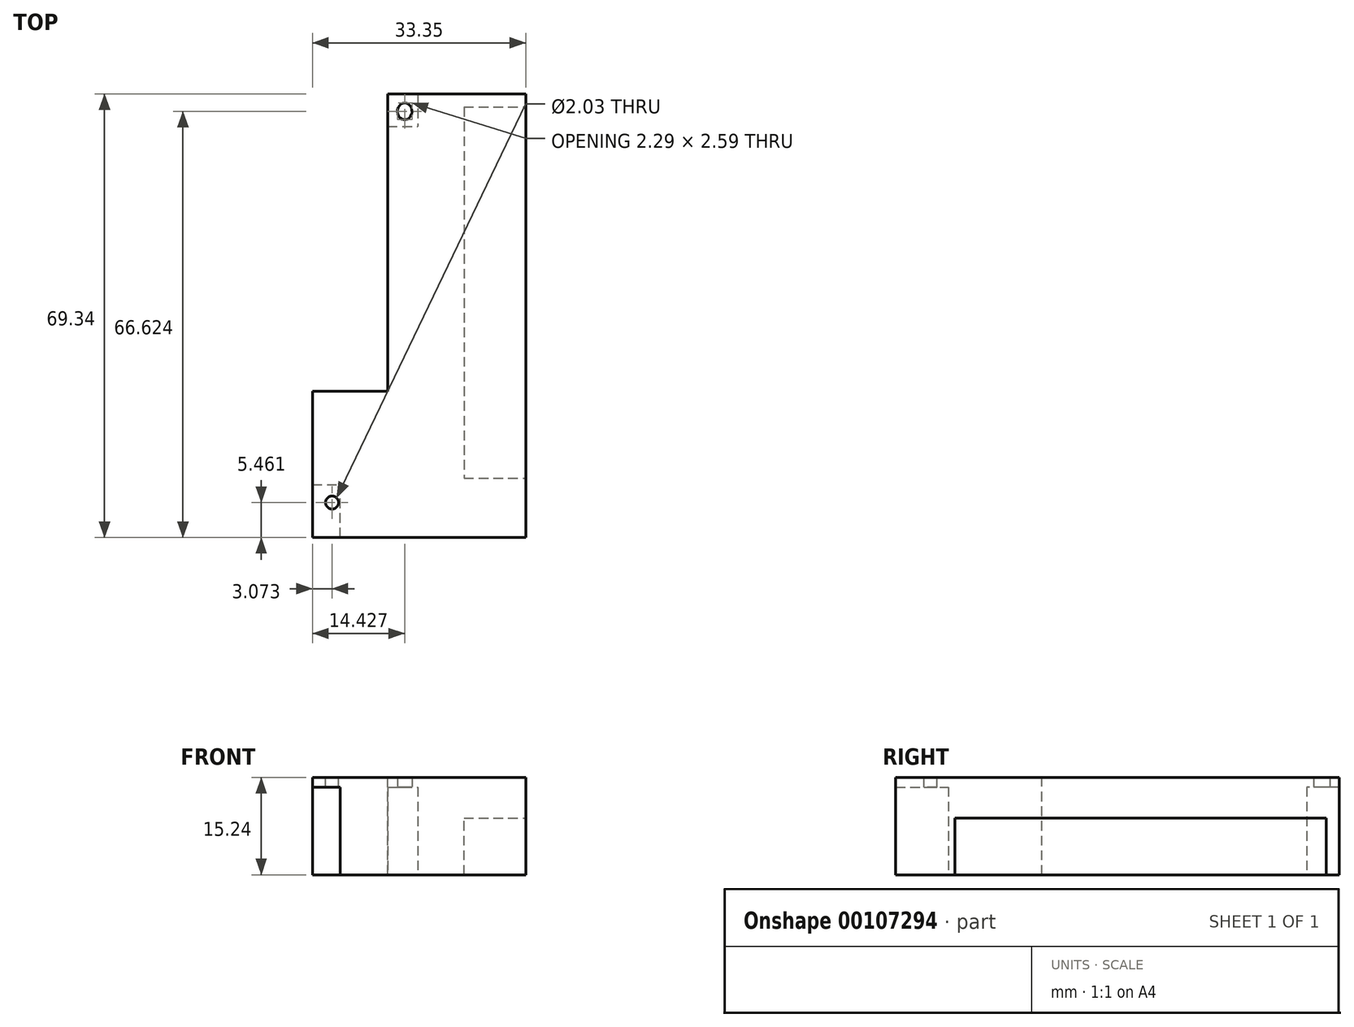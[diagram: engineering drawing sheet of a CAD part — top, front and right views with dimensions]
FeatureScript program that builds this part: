
annotation { "Feature Type Name" : "Feature", "Feature Type Description" : "" }
export const myFeature = defineFeature(function(context is Context, id is Id, definition is map)
    precondition{}
    {
        {
            var Q0;
            Q0=qCreatedBy(makeId("Top.planeOp"),FACE);
            var sketch = newSketch(context, id + "F0", { "sketchPlane" : qUnion([Q0])});
            skLineSegment(sketch, "E0.bottom", {"start": v(-21.6, 69.34) * mm, "end": v(0, 69.34) * mm});
            skLineSegment(sketch, "E0.top", {"start": v(-21.6, 0) * mm, "end": v(0, 0) * mm});
            skLineSegment(sketch, "E0.left", {"start": v(-21.6, 69.34) * mm, "end": v(-21.6, 22.86) * mm});
            skLineSegment(sketch, "E0.right", {"start": v(0, 69.34) * mm, "end": v(0, 0) * mm});
            skLineSegment(sketch, "E1.bottom", {"start": v(-21.6, 0) * mm, "end": v(-33.35, 0) * mm});
            skLineSegment(sketch, "E1.top", {"start": v(-21.6, 22.86) * mm, "end": v(-33.35, 22.86) * mm});
            skLineSegment(sketch, "E1.right", {"start": v(-33.35, 0) * mm, "end": v(-33.35, 22.86) * mm});
            skCircle(sketch, "E2", {"center": v(-30.28, 5.46) * mm, "radius": 1.02 * mm});
            skLineSegment(sketch, "E3", {"start": v(-33.35, 9.14) * mm, "end": v(0, 9.14) * mm});
            skEllipse(sketch, "E4", {"center": v(-18.92, 66.62) * mm, "majorRadius": 1.3 * mm, "minorRadius": 1.14 * mm, "majorAxis": v(0, 1)});
            skSolve(sketch);
        }
        {
            var Q0;
            {var subQ2=sQuery(id+"F0.wireOp",EDGE,"E0.bottom");Q0=makeQuery(id+"F0.imprint","IMPRINT",FACE,{"disambiguationData":[TD([[makeQuery(id+"F0.imprint","IMPRINT",EDGE,{"derivedFrom":subQ2}),-1.0]])]});}
            var Q1;
            {var subQ4=sQuery(id+"F0.wireOp",EDGE,"E0.top");Q1=makeQuery(id+"F0.imprint","IMPRINT",FACE,{"disambiguationData":[TD([[makeQuery(id+"F0.imprint","IMPRINT",EDGE,{"derivedFrom":subQ4}),1.0]])]});}
            extrude(context, id + "F1", {"entities" : qUnion([Q0, Q1]), "oppositeDirection" : true, "depth" : 15.24 * mm});
        }
        {
            var Q0;
            Q0=makeQuery(id+"F1.opExtrude","CAP_FACE",FACE,{"disambiguationData":[OSD([sQuery(id+"F0.wireOp",EDGE,"E0.bottom"),sQuery(id+"F0.wireOp",EDGE,"E0.top"),sQuery(id+"F0.wireOp",EDGE,"E0.left"),sQuery(id+"F0.wireOp",EDGE,"E0.right"),sQuery(id+"F0.wireOp",EDGE,"E1.bottom"),sQuery(id+"F0.wireOp",EDGE,"E1.top"),sQuery(id+"F0.wireOp",EDGE,"E1.right"),sQuery(id+"F0.wireOp",EDGE,"E2"),sQuery(id+"F0.wireOp",EDGE,"E4")])],"isStart":false});
            var sketch = newSketch(context, id + "F2", { "sketchPlane" : qUnion([Q0])});
            skLineSegment(sketch, "E5.bottom", {"start": v(-33.35, 0) * mm, "end": v(-29.03, 0) * mm});
            skLineSegment(sketch, "E5.top", {"start": v(-33.35, -8.26) * mm, "end": v(-29.03, -8.26) * mm});
            skLineSegment(sketch, "E5.left", {"start": v(-33.35, 0) * mm, "end": v(-33.35, -8.26) * mm});
            skLineSegment(sketch, "E5.right", {"start": v(-29.03, 0) * mm, "end": v(-29.03, -8.26) * mm});
            skSolve(sketch);
        }
        {
            var Q0;
            Q0=makeQuery(id+"F2.imprint","IMPRINT",FACE,{"disambiguationData":[TD([[makeQuery(id+"F2.imprint","IMPRINT",EDGE,{"derivedFrom":sQuery(id+"F2.wireOp",EDGE,"E5.bottom")}),1.0]])]});
            extrude(context, id + "F3", {"entities" : qUnion([Q0]), "operationType" : NewBodyOperationType.REMOVE, "oppositeDirection" : true, "depth" : 13.72 * mm});
        }
        {
            var Q0;
            Q0=makeQuery(id+"F1.opExtrude","CAP_FACE",FACE,{"disambiguationData":[OSD([sQuery(id+"F0.wireOp",EDGE,"E0.bottom"),sQuery(id+"F0.wireOp",EDGE,"E0.top"),sQuery(id+"F0.wireOp",EDGE,"E0.left"),sQuery(id+"F0.wireOp",EDGE,"E0.right"),sQuery(id+"F0.wireOp",EDGE,"E1.bottom"),sQuery(id+"F0.wireOp",EDGE,"E1.top"),sQuery(id+"F0.wireOp",EDGE,"E1.right"),sQuery(id+"F0.wireOp",EDGE,"E2"),sQuery(id+"F0.wireOp",EDGE,"E4")])],"isStart":false});
            var sketch = newSketch(context, id + "F4", { "sketchPlane" : qUnion([Q0])});
            skLineSegment(sketch, "E6.bottom", {"start": v(-21.6, -69.34) * mm, "end": v(-16.9, -69.34) * mm});
            skLineSegment(sketch, "E6.top", {"start": v(-21.6, -64.26) * mm, "end": v(-16.9, -64.26) * mm});
            skLineSegment(sketch, "E6.left", {"start": v(-21.6, -69.34) * mm, "end": v(-21.6, -64.26) * mm});
            skLineSegment(sketch, "E6.right", {"start": v(-16.9, -69.34) * mm, "end": v(-16.9, -64.26) * mm});
            skSolve(sketch);
        }
        {
            var Q0;
            Q0=qSketchRegion(id+"F4",true);
            extrude(context, id + "F5", {"entities" : qUnion([Q0]), "operationType" : NewBodyOperationType.REMOVE, "oppositeDirection" : true, "depth" : 13.72 * mm});
        }
        {
            var Q0;
            Q0=makeQuery(id+"F1.opExtrude","SWEPT_FACE",FACE,{"disambiguationData":[OSD([sQuery(id+"F0.wireOp",EDGE,"E0.right")])]});
            var sketch = newSketch(context, id + "F6", { "sketchPlane" : qUnion([Q0])});
            skLineSegment(sketch, "E7.bottom", {"start": v(9.27, -15.24) * mm, "end": v(67.3, -15.24) * mm});
            skLineSegment(sketch, "E7.top", {"start": v(9.27, -6.35) * mm, "end": v(67.3, -6.35) * mm});
            skLineSegment(sketch, "E7.left", {"start": v(9.27, -15.24) * mm, "end": v(9.27, -6.35) * mm});
            skLineSegment(sketch, "E7.right", {"start": v(67.3, -15.24) * mm, "end": v(67.3, -6.35) * mm});
            skSolve(sketch);
        }
        {
            var Q0;
            Q0=makeQuery(id+"F6.imprint","IMPRINT",FACE,{"disambiguationData":[TD([[makeQuery(id+"F6.imprint","IMPRINT",EDGE,{"derivedFrom":sQuery(id+"F6.wireOp",EDGE,"E7.bottom")}),-1.0]])]});
            extrude(context, id + "F7", {"entities" : qUnion([Q0]), "operationType" : NewBodyOperationType.REMOVE, "oppositeDirection" : true, "depth" : 9.65 * mm});
        }
    });
